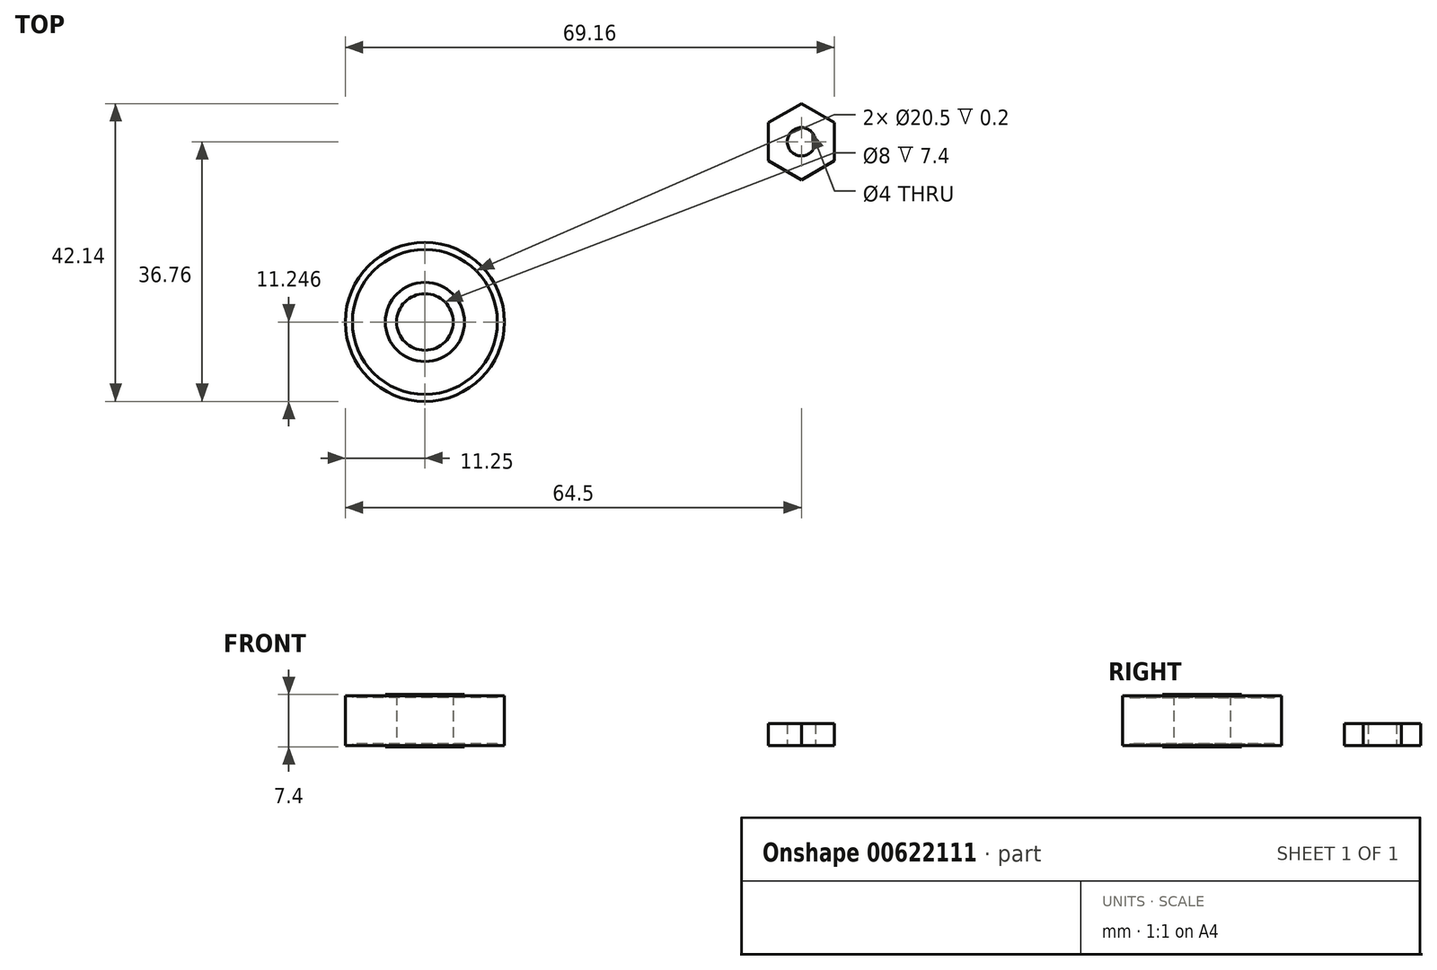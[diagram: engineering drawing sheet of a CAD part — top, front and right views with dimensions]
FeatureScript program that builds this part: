
annotation { "Feature Type Name" : "Feature", "Feature Type Description" : "" }
export const myFeature = defineFeature(function(context is Context, id is Id, definition is map)
    precondition{}
    {
        {
            var Q0;
            Q0=qCreatedBy(makeId("Top.planeOp"),FACE);
            var sketch = newSketch(context, id + "F0", { "sketchPlane" : qUnion([Q0])});
            skCircle(sketch, "E0.cCircle", {"center": v(0, 0) * mm, "radius": 4.66 * mm, "construction": true});
            skLineSegment(sketch, "E0.0", {"start": v(4.66, 2.7) * mm, "end": v(4.66, -2.7) * mm});
            skLineSegment(sketch, "E0.1", {"start": v(4.66, -2.7) * mm, "end": v(0, -5.38) * mm});
            skLineSegment(sketch, "E0.2", {"start": v(0, -5.38) * mm, "end": v(-4.66, -2.7) * mm});
            skLineSegment(sketch, "E0.3", {"start": v(-4.66, -2.7) * mm, "end": v(-4.66, 2.7) * mm});
            skLineSegment(sketch, "E0.4", {"start": v(-4.66, 2.7) * mm, "end": v(0, 5.38) * mm});
            skLineSegment(sketch, "E0.5", {"start": v(0, 5.38) * mm, "end": v(4.66, 2.7) * mm});
            skPoint(sketch, "E0.0.midPoint", {"position": v(4.66, 0) * mm});
            skCircle(sketch, "E1", {"center": v(0, 0) * mm, "radius": 2 * mm});
            skSolve(sketch);
        }
        {
            var Q0;
            Q0=makeQuery(id+"F0.imprint","IMPRINT",FACE,{"disambiguationData":[TD([[makeQuery(id+"F0.imprint","IMPRINT",EDGE,{"derivedFrom":sQuery(id+"F0.wireOp",EDGE,"E0.0")}),-1.0]])]});
            extrude(context, id + "F1", {"entities" : qUnion([Q0]), "depth" : 3.1 * mm, "offsetDistance" : 25 * mm});
        }
        {
            var Q0;
            Q0=qCreatedBy(makeId("Top.planeOp"),FACE);
            var sketch = newSketch(context, id + "F2", { "sketchPlane" : qUnion([Q0])});
            skCircle(sketch, "E2", {"center": v(-53.25, -25.51) * mm, "radius": 11.25 * mm});
            skCircle(sketch, "E3", {"center": v(-53.25, -25.51) * mm, "radius": 4 * mm});
            skCircle(sketch, "E4", {"center": v(-53.25, -25.51) * mm, "radius": 5.6 * mm});
            skCircle(sketch, "E5", {"center": v(-53.25, -25.51) * mm, "radius": 10.25 * mm});
            skLineSegment(sketch, "E6", {"start": v(-53.25, -25.51) * mm, "end": v(-42, -25.51) * mm});
            skLineSegment(sketch, "E7", {"start": v(-42, -25.51) * mm, "end": v(-43, -25.51) * mm});
            skSolve(sketch);
        }
        {
            var Q0;
            Q0=makeQuery(id+"F2.imprint","IMPRINT",FACE,{"disambiguationData":[TD([[makeQuery(id+"F2.imprint","IMPRINT",EDGE,{"derivedFrom":sQuery(id+"F2.wireOp",EDGE,"E2")}),1.0]])]});
            extrude(context, id + "F3", {"entities" : qUnion([Q0]), "depth" : 7 * mm, "offsetDistance" : 25 * mm});
        }
        {
            var Q0;
            Q0=makeQuery(id+"F2.imprint","IMPRINT",FACE,{"disambiguationData":[TD([[makeQuery(id+"F2.imprint","IMPRINT",EDGE,{"derivedFrom":sQuery(id+"F2.wireOp",EDGE,"E4")}),-1.0]])]});
            extrude(context, id + "F4", {"entities" : qUnion([Q0]), "operationType" : NewBodyOperationType.ADD, "depth" : 6.8 * mm, "offsetDistance" : 25 * mm, "hasSecondDirection" : true, "secondDirectionOppositeDirection" : false, "secondDirectionDepth" : .2 * mm});
        }
        {
            var Q0;
            Q0=makeQuery(id+"F2.imprint","IMPRINT",FACE,{"disambiguationData":[TD([[makeQuery(id+"F2.imprint","IMPRINT",EDGE,{"derivedFrom":sQuery(id+"F2.wireOp",EDGE,"E3")}),-1.0]])]});
            extrude(context, id + "F5", {"entities" : qUnion([Q0]), "operationType" : NewBodyOperationType.ADD, "depth" : 7.2 * mm, "offsetDistance" : 25 * mm, "hasSecondDirection" : true, "secondDirectionOppositeDirection" : true, "secondDirectionDepth" : 0.2 * mm});
        }
    });
